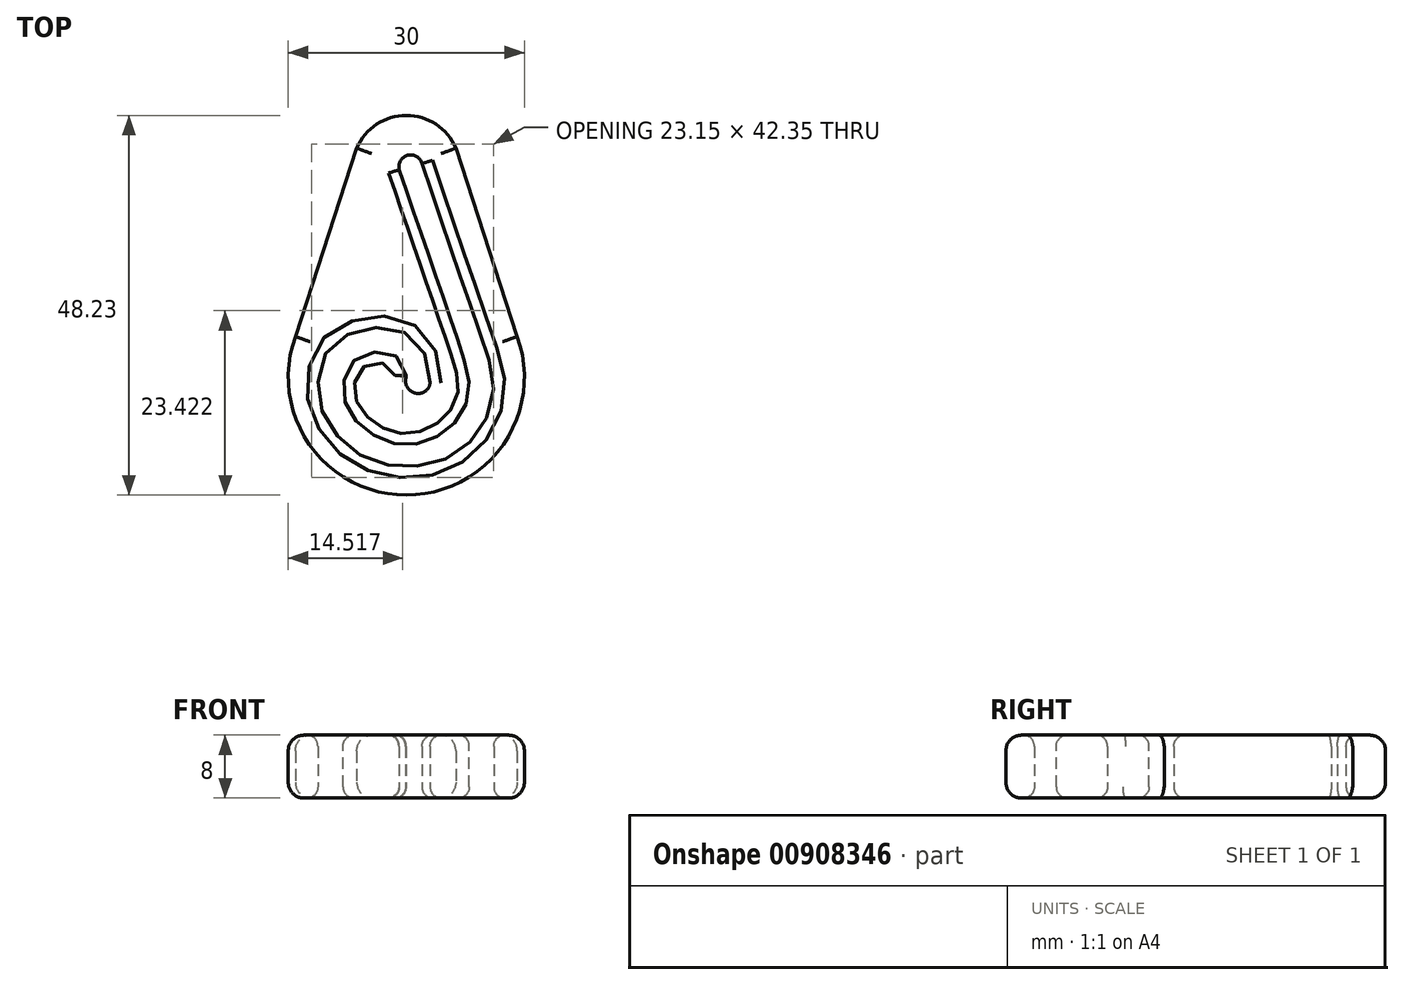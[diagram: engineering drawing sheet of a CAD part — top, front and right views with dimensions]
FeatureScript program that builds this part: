
annotation { "Feature Type Name" : "Feature", "Feature Type Description" : "" }
export const myFeature = defineFeature(function(context is Context, id is Id, definition is map)
    precondition{}
    {
        {
            var Q0;
            Q0=qCreatedBy(makeId("Top.planeOp"),FACE);
            var sketch = newSketch(context, id + "F0", { "sketchPlane" : qUnion([Q0])});
            skArc(sketch, "E0", {"start": v(-14.1, 5.13) * mm, "mid": v(0, -15) * mm, "end": v(14.1, 5.13) * mm});
            skPoint(sketch, "E1.start.orphan", {"position": v(0, 26.39) * mm});
            skLineSegment(sketch, "E2", {"start": v(0, 0) * mm, "end": v(0, 0) * mm});
            skArc(sketch, "E3", {"start": v(0, 0) * mm, "mid": v(1, -2) * mm, "end": v(3, -1.02) * mm});
            skLineSegment(sketch, "E4", {"start": v(-6.3, 29.08) * mm, "end": v(-14.1, 5.13) * mm});
            skLineSegment(sketch, "E5", {"start": v(6.3, 29.08) * mm, "end": v(14.1, 5.13) * mm});
            skLineSegment(sketch, "E6", {"start": v(-8, -2.23) * mm, "end": v(-8, -2.23) * mm});
            skArc(sketch, "E7", {"start": v(6.3, 29.08) * mm, "mid": v(0, 33.23) * mm, "end": v(-6.3, 29.08) * mm});
            skFitSpline(sketch, "E8", {"points": [v(3, -1.02) * mm, v(1.06, 4.8) * mm, v(-4.1, 6.3) * mm, v(-8.98, 4.49) * mm, v(-10.8, 1.66) * mm, v(-11.14, -2.86) * mm, v(-9.77, -6.06) * mm, v(-5.36, -10.17) * mm, v(3.6, -10.92) * mm, v(9.55, -6.41) * mm, v(11.11, -1.3) * mm, v(9.86, 4.08) * mm, v(2, 27.12) * mm], "startDerivative": vector(6.66, 79.76) * mm, "endDerivative": vector(-55.2, 168.14) * mm});
            skFitSpline(sketch, "E9", {"points": [v(0, 0) * mm, v(-0.4, 1.66) * mm, v(-1.66, 2.84) * mm, v(-6.24, 2.44) * mm, v(-8, -2.23) * mm, v(-5.37, -6.57) * mm, v(0, -8.6) * mm, v(5.56, -6.38) * mm, v(7.92, -2.23) * mm, v(6.93, 3.45) * mm, v(-0.9, 26.33) * mm], "startDerivative": vector(0, 57.6) * mm, "endDerivative": vector(-42.27, 124.28) * mm});
            skArc(sketch, "E10", {"start": v(2, 27.12) * mm, "mid": v(0.16, 28.16) * mm, "end": v(-0.9, 26.33) * mm});
            skSolve(sketch);
        }
        {
            var Q0;
            Q0=makeQuery(id+"F0.imprint","IMPRINT",FACE,{"disambiguationData":[TD([[makeQuery(id+"F0.imprint","IMPRINT",EDGE,{"derivedFrom":sQuery(id+"F0.wireOp",EDGE,"E0")}),1.0]])]});
            extrude(context, id + "F1", {"entities" : qUnion([Q0]), "depth" : 8 * mm, "offsetDistance" : 25 * mm});
        }
        {
            var Q0;
            Q0=makeQuery(id+"F1.opExtrude","CAP_EDGE",EDGE,{"disambiguationData":[OSD([sQuery(id+"F0.wireOp",EDGE,"4c46b97f-c5b4-4793-96a7-fe9158ad3d56")])],"isStart":false});
            var Q1;
            Q1=makeQuery(id+"F1.opExtrude","CAP_EDGE",EDGE,{"disambiguationData":[OSD([sQuery(id+"F0.wireOp",EDGE,"CfmwiIhC-c1y3-zuAX-zMKs-NfLKIyrCQDV9")])],"isStart":false});
            var Q2;
            Q2=makeQuery(id+"F1.opExtrude","CAP_EDGE",EDGE,{"disambiguationData":[OSD([sQuery(id+"F0.wireOp",EDGE,"bb0fb741-8d50-44b2-94b8-18b45131e533")])],"isStart":false});
            var Q3;
            Q3=makeQuery(id+"F1.opExtrude","CAP_EDGE",EDGE,{"disambiguationData":[OSD([sQuery(id+"F0.wireOp",EDGE,"E0")])],"isStart":false});
            var Q4;
            Q4=makeQuery(id+"F1.opExtrude","CAP_EDGE",EDGE,{"disambiguationData":[OSD([sQuery(id+"F0.wireOp",EDGE,"E0")])],"isStart":true});
            var Q5;
            Q5=makeQuery(id+"F1.opExtrude","CAP_EDGE",EDGE,{"disambiguationData":[OSD([sQuery(id+"F0.wireOp",EDGE,"bb0fb741-8d50-44b2-94b8-18b45131e533")])],"isStart":true});
            var Q6;
            Q6=makeQuery(id+"F1.opExtrude","CAP_EDGE",EDGE,{"disambiguationData":[OSD([sQuery(id+"F0.wireOp",EDGE,"4c46b97f-c5b4-4793-96a7-fe9158ad3d56")])],"isStart":true});
            var Q7;
            Q7=makeQuery(id+"F1.opExtrude","CAP_EDGE",EDGE,{"disambiguationData":[OSD([sQuery(id+"F0.wireOp",EDGE,"CfmwiIhC-c1y3-zuAX-zMKs-NfLKIyrCQDV9")])],"isStart":true});
            var Q8;
            Q8=makeQuery(id+"F1.opExtrude","CAP_EDGE",EDGE,{"disambiguationData":[OSD([sQuery(id+"F0.wireOp",EDGE,"E7")])],"isStart":false});
            var Q9;
            Q9=makeQuery(id+"F1.opExtrude","CAP_EDGE",EDGE,{"disambiguationData":[OSD([sQuery(id+"F0.wireOp",EDGE,"E7")])],"isStart":true});
            fillet(context, id + "F2", {"entities" : qUnion([Q0, Q1, Q2, Q3, Q4, Q5, Q6, Q7, Q8, Q9]), "radius" : 2 * mm, "tangentPropagation" : true, "allowEdgeOverflow" : false});
        }
        {
            var Q0;
            {var subQ0=sQuery(id+"F0.wireOp",EDGE,"82d18ad7-a181-48e3-bed3-589e201e7fcc");Q0=makeQuery(id+"F1.opExtrude","CAP_EDGE",EDGE,{"disambiguationData":[OSD([subQ0]),TDD([makeQuery(id+"F0.imprint","IMPRINT",EDGE,{"disambiguationData":[TD([[makeQuery(id+"F0.imprint","INTERSECT",VERTEX,{"derivedFrom":[sQuery(id+"F0.wireOp",EDGE,"dgkHKLtj-J6tY-MyBF-vRL6-yoZuAsEvQvpc"),subQ0]}),-1.0]])],"derivedFrom":subQ0})])],"isStart":true});}
            var Q1;
            Q1=makeQuery(id+"F1.opExtrude","CAP_EDGE",EDGE,{"disambiguationData":[OSD([sQuery(id+"F0.wireOp",EDGE,"41fcc7f6-c8d6-45e7-9f7e-b4285f1a0514")])],"isStart":true});
            var Q2;
            Q2=makeQuery(id+"F1.opExtrude","CAP_EDGE",EDGE,{"disambiguationData":[OSD([sQuery(id+"F0.wireOp",EDGE,"HtF0ZHnT-36mG-WQkg-tRtk-7PdODIJdWa8L")])],"isStart":true});
            var Q3;
            {var subQ0=sQuery(id+"F0.wireOp",EDGE,"82d18ad7-a181-48e3-bed3-589e201e7fcc");Q3=makeQuery(id+"F1.opExtrude","CAP_EDGE",EDGE,{"disambiguationData":[OSD([subQ0]),TDD([makeQuery(id+"F0.imprint","IMPRINT",EDGE,{"disambiguationData":[TD([[makeQuery(id+"F0.imprint","INTERSECT",VERTEX,{"derivedFrom":[sQuery(id+"F0.wireOp",EDGE,"RZ7SsEPt-vcVz-EwQr-BuGM-gbgMcMgmB998"),subQ0]}),1.0]])],"derivedFrom":subQ0})])],"isStart":true});}
            var Q4;
            Q4=makeQuery(id+"F1.opExtrude","CAP_EDGE",EDGE,{"disambiguationData":[OSD([sQuery(id+"F0.wireOp",EDGE,"dgkHKLtj-J6tY-MyBF-vRL6-yoZuAsEvQvpc")])],"isStart":true});
            var Q5;
            Q5=makeQuery(id+"F1.opExtrude","CAP_EDGE",EDGE,{"disambiguationData":[OSD([sQuery(id+"F0.wireOp",EDGE,"E3")])],"isStart":true});
            var Q6;
            Q6=makeQuery(id+"F1.opExtrude","CAP_EDGE",EDGE,{"disambiguationData":[OSD([sQuery(id+"F0.wireOp",EDGE,"82d18ad7-a181-48e3-bed3-589e201e7fcc")])],"isStart":false});
            var Q7;
            Q7=makeQuery(id+"F1.opExtrude","SWEPT_EDGE",EDGE,{"disambiguationData":[OSD([sQuery(id+"F0.wireOp",EDGE,"82d18ad7-a181-48e3-bed3-589e201e7fcc"),sQuery(id+"F0.wireOp",EDGE,"E3")])]});
            var Q8;
            Q8=makeQuery(id+"F1.opExtrude","CAP_EDGE",EDGE,{"disambiguationData":[OSD([sQuery(id+"F0.wireOp",EDGE,"41fcc7f6-c8d6-45e7-9f7e-b4285f1a0514")])],"isStart":false});
            var Q9;
            Q9=makeQuery(id+"F1.opExtrude","CAP_EDGE",EDGE,{"disambiguationData":[OSD([sQuery(id+"F0.wireOp",EDGE,"E8")])],"isStart":true});
            var Q10;
            Q10=makeQuery(id+"F1.opExtrude","CAP_EDGE",EDGE,{"disambiguationData":[OSD([sQuery(id+"F0.wireOp",EDGE,"E10")])],"isStart":true});
            var Q11;
            Q11=makeQuery(id+"F1.opExtrude","CAP_FACE",FACE,{"disambiguationData":[OSD([sQuery(id+"F0.wireOp",EDGE,"E0"),sQuery(id+"F0.wireOp",EDGE,"E3"),sQuery(id+"F0.wireOp",EDGE,"E4"),sQuery(id+"F0.wireOp",EDGE,"E5"),sQuery(id+"F0.wireOp",EDGE,"E7"),sQuery(id+"F0.wireOp",EDGE,"E8"),sQuery(id+"F0.wireOp",EDGE,"E9"),sQuery(id+"F0.wireOp",EDGE,"E10")])],"isStart":true});
            var Q12;
            Q12=makeQuery(id+"F1.opExtrude","CAP_EDGE",EDGE,{"disambiguationData":[OSD([sQuery(id+"F0.wireOp",EDGE,"E9")])],"isStart":true});
            var Q13;
            Q13=makeQuery(id+"F1.opExtrude","CAP_EDGE",EDGE,{"disambiguationData":[OSD([sQuery(id+"F0.wireOp",EDGE,"E8")])],"isStart":false});
            var Q14;
            Q14=makeQuery(id+"F1.opExtrude","CAP_EDGE",EDGE,{"disambiguationData":[OSD([sQuery(id+"F0.wireOp",EDGE,"E9")])],"isStart":false});
            var Q15;
            Q15=makeQuery(id+"F1.opExtrude","SWEPT_FACE",FACE,{"disambiguationData":[OSD([sQuery(id+"F0.wireOp",EDGE,"E3")])]});
            fillet(context, id + "F3", {"entities" : qUnion([Q0, Q1, Q2, Q3, Q4, Q5, Q6, Q7, Q8, Q9, Q10, Q11, Q12, Q13, Q14, Q15]), "radius" : 1.4 * mm, "tangentPropagation" : true, "allowEdgeOverflow" : false});
        }
    });
